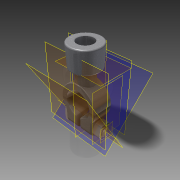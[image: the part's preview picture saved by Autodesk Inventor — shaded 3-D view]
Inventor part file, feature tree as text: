
AUTODESK INVENTOR PART (.ipt)
format: ipt  version: 2014 (Build 180170000, 170)  size: 491,008 bytes
history: native  units: in
note: dims shown in document units (in); Inventor stores cm internally (conversion verified against a paired STEP export)
features: sketch x11, projected_geometry x10, plane x8, extrude x7, fillet x7, other x3, revolve x2, hole x1, thread x1, chamfer x1, surface_op x1, mirror x1, reference x1
ambient origin geometry x8: Origin, YZ Plane, XZ Plane, XY Plane, X Axis, Y Axis, Z Axis, Center Point
bodies: Solid1 (feature_tree), Solid3 (feature_tree), Solid5 (feature_tree)
feature tree (54):
  extrude  "Extrusion1"  Depth=0.125in
  fillet  "Fillet1"  Radius=0.5in
  hole  "Hole1"  [1 undecoded]
  plane  "Work Plane1"
  extrude  "Extrusion6"  Depth=0.15in TaperAngle=0.0deg
  plane  "Work Plane2"
  sketch  "Sketch8"  dims[d19=0.0625in d28=0.15in d29=0.0in]
  other  "Work Axis1"
  revolve  "Revolution2"  [1 undecoded]
  fillet  "Fillet2"  Radius=0.01in
  fillet  "Fillet3"  Radius=0.2in
  extrude  "Extrusion7"  Depth=0.035in
  plane  "Work Plane3"
  revolve  "Revolution3"  [1 undecoded]
  plane  "Work Plane5"
  extrude  "Extrusion8"  Depth=0.125in
  thread  "Thread1"  [1 undecoded]
  chamfer  "Chamfer1"  Distance=0.75in
  plane  "Work Plane7"
  plane  "Work Plane8"
  fillet  "Fillet6"  Radius=0.75in
  fillet  "Fillet7"  Radius=0.5625in
  surface_op  "Sculpt1"
  plane  "Work Plane9"
  mirror  "Mirror3"
  plane  "Work Plane10"
  extrude  "Extrusion11"  Depth=0.035in TaperAngle=0.0deg
  extrude  "Extrusion12"  Depth=0.035in
  extrude  "Extrusion13"  Depth=0.035in
  fillet  "Fillet9"  [1 undecoded]
  fillet  "Fillet10"  [1 undecoded]
  sketch  "Sketch1"  dims[d0=0.15in d1=0.125in d7=0.5in d8=0.0in]
  reference  "Reference1"
  sketch  "Sketch2"  dims[d9=0.2in]
  projected_geometry  "Projected Loop1"
  sketch  "Sketch7"  dims[d10=0.25in d11=0.75in d12=0.375in d13=0.25in d14=0.5635in d15=1.0in d16=0.8108in d17=0.315in]
  projected_geometry  "Projected Loop5"
  sketch  "Sketch9"  dims[d30=90.0deg d31=0.02in d32=0.01in d33=0.2in d34=0.0in]
  projected_geometry  "Projected Loop6"
  projected_geometry  "Projected Loop7"
  sketch  "Sketch10"  dims[d35=90.0deg d36=0.035in]
  sketch  "Sketch11"  dims[d37=0.2in d38=0.0in d39=1.0in d40=0.0in]
  projected_geometry  "Projected Loop8"
  projected_geometry  "Projected Loop9"
  sketch  "Sketch12"  dims[d41=0.02in d42=0.125in d43=45.0deg d53=0.0625in d58=0.1in]
  sketch  "Sketch16"  dims[d59=0.02in]
  projected_geometry  "Projected Loop12"
  sketch  "Sketch17"  dims[d61=0.8125in]
  projected_geometry  "Projected Loop13"
  sketch  "Sketch18"  dims[d62=0.0625in d63=0.75in d64=0.0in d65=0.75in d66=0.5625in d67=0.0172in d68=0.1in d69=0.0in d70=0.035in d71=0.035in]
  projected_geometry  "Projected Loop14"
  projected_geometry  "Project Cut Edges1"
  other  "Composite1"
  other  "Srf1"
note: 6 required parameter values undecoded (feature->parameter linkage not recoverable at this tier; creation-order binding heuristic only, values carry confidence <= 0.55)